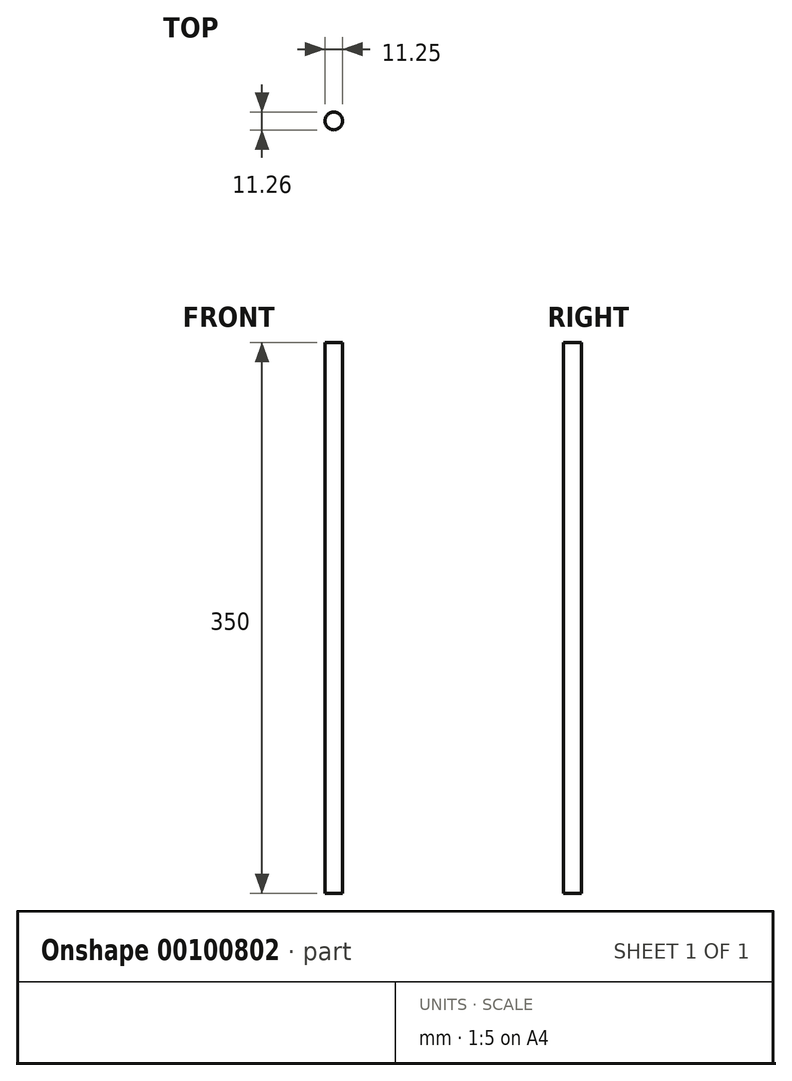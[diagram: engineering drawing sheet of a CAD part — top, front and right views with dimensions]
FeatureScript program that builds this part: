
annotation { "Feature Type Name" : "Feature", "Feature Type Description" : "" }
export const myFeature = defineFeature(function(context is Context, id is Id, definition is map)
    precondition{}
    {
        {
            var Q0;
            Q0=qCreatedBy(makeId("Top.planeOp"),FACE);
            var sketch = newSketch(context, id + "F0", { "sketchPlane" : qUnion([Q0])});
            skCircle(sketch, "E0", {"center": v(-41.22, 0) * mm, "radius": 5.62 * mm});
            skSolve(sketch);
        }
        {
            var Q0;
            Q0=sQuery(id+"F0.wireOp",EDGE,"E0");
            extrude(context, id + "F1", {"bodyType" : ToolBodyType.SURFACE, "surfaceEntities" : qUnion([Q0]), "depth" : 350 * mm});
        }
    });
